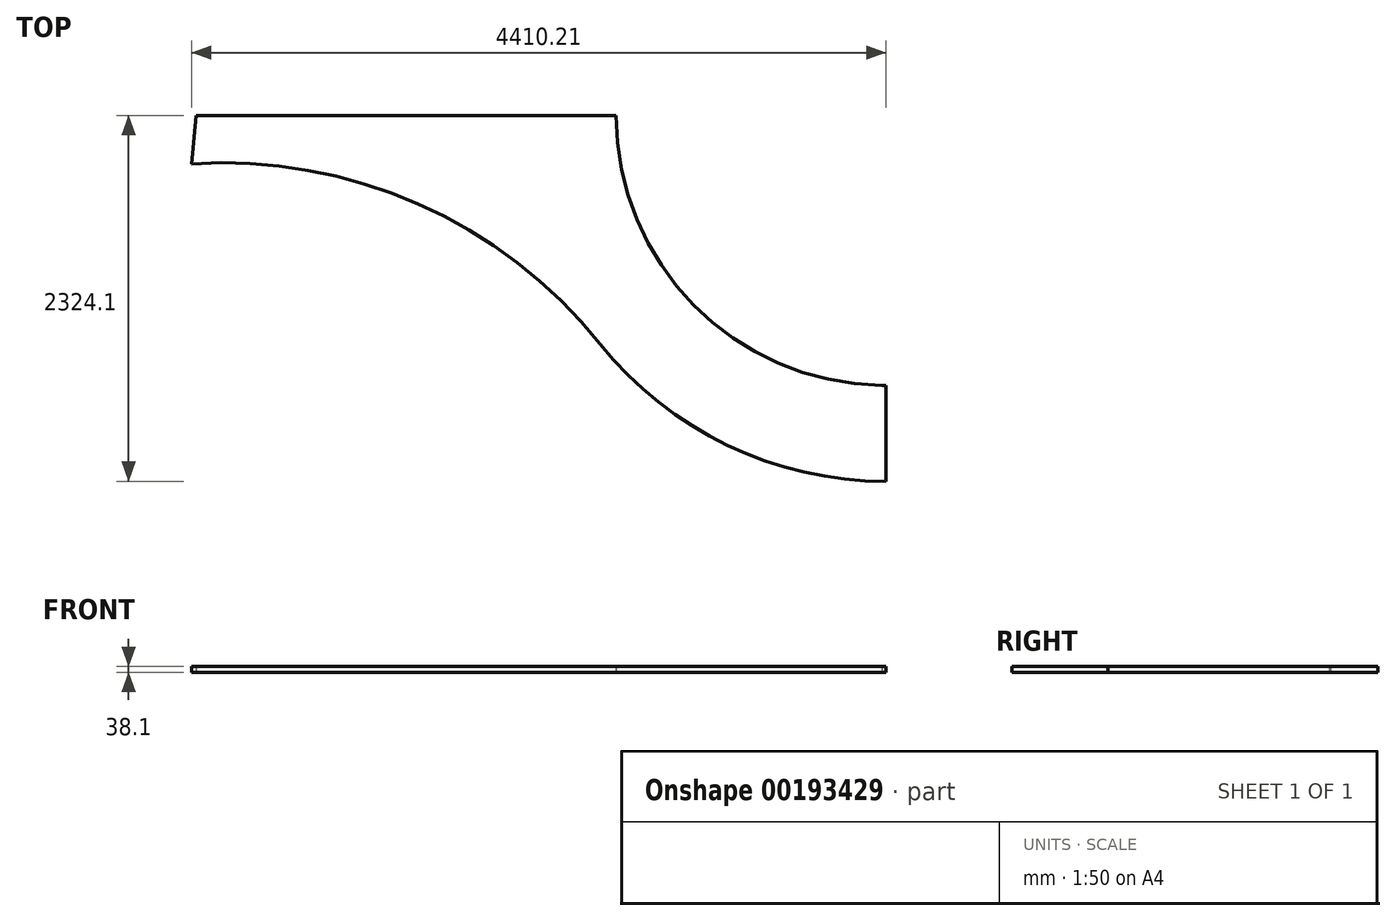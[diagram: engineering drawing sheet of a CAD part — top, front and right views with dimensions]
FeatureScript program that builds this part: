
annotation { "Feature Type Name" : "Feature", "Feature Type Description" : "" }
export const myFeature = defineFeature(function(context is Context, id is Id, definition is map)
    precondition{}
    {
        {
            var Q0;
            Q0=qCreatedBy(makeId("Top.planeOp"),FACE);
            var sketch = newSketch(context, id + "F0", { "sketchPlane" : qUnion([Q0])});
            skLineSegment(sketch, "E0", {"start": v(-2316.67, 127.82) * mm, "end": v(349.93, 127.82) * mm});
            skLineSegment(sketch, "E1", {"start": v(2064.43, -1586.68) * mm, "end": v(2064.43, -2196.28) * mm});
            skArc(sketch, "E2", {"start": v(2064.43, -1586.68) * mm, "mid": v(852.1, -1084.52) * mm, "end": v(349.93, 127.82) * mm});
            skArc(sketch, "E3.0", {"start": v(2064.43, -1891.48) * mm, "mid": v(1189.8, -1692.24) * mm, "end": v(487.77, -1133.82) * mm});
            skArc(sketch, "E4.0", {"start": v(2064.43, -2196.28) * mm, "mid": v(1057.78, -1966.96) * mm, "end": v(249.79, -1324.25) * mm});
            skLineSegment(sketch, "E5", {"start": v(-2316.67, 127.82) * mm, "end": v(-2345.78, -179.16) * mm});
            skPoint(sketch, "E6", {"position": v(-2316.67, 127.82) * mm});
            skArc(sketch, "E7", {"start": v(487.77, -1133.82) * mm, "mid": v(-608.98, -238.62) * mm, "end": v(-1976.45, 127.82) * mm});
            skArc(sketch, "E8.0", {"start": v(249.79, -1324.25) * mm, "mid": v(-907.75, -433.81) * mm, "end": v(-2345.78, -179.16) * mm});
            skPoint(sketch, "E9.orphan", {"position": v(-2436.3, -1133.82) * mm});
            skLineSegment(sketch, "E10.0", {"start": v(-2291.3, 126.27) * mm, "end": v(-2317.7, -152.02) * mm});
            skArc(sketch, "E11.0", {"start": v(300.99, -1348.25) * mm, "mid": v(-872.47, -421.75) * mm, "end": v(-2343.36, -153.55) * mm});
            skArc(sketch, "E12.0", {"start": v(2064.43, -2170.88) * mm, "mid": v(1097.91, -1957.81) * mm, "end": v(310.57, -1358.11) * mm});
            skLineSegment(sketch, "E13.0", {"start": v(2039.03, -1586.5) * mm, "end": v(2039.03, -2170.74) * mm});
            skLineSegment(sketch, "E14", {"start": v(-2343.36, -153.55) * mm, "end": v(-2316.67, 127.82) * mm});
            skLineSegment(sketch, "E15", {"start": v(-2343.36, -153.55) * mm, "end": v(-2317.7, -152.02) * mm});
            skLineSegment(sketch, "E16", {"start": v(-2291.3, 126.27) * mm, "end": v(-2316.67, 127.82) * mm});
            skLineSegment(sketch, "E17.bottom", {"start": v(2039.03, -1586.5) * mm, "end": v(2064.43, -1586.5) * mm});
            skLineSegment(sketch, "E17.top", {"start": v(2039.03, -1586.68) * mm, "end": v(2064.43, -1586.68) * mm});
            skLineSegment(sketch, "E17.left", {"start": v(2039.03, -1586.5) * mm, "end": v(2039.03, -1586.68) * mm});
            skLineSegment(sketch, "E17.right", {"start": v(2064.43, -1586.5) * mm, "end": v(2064.43, -1586.68) * mm});
            skLineSegment(sketch, "E18", {"start": v(2064.43, -2170.88) * mm, "end": v(2039.03, -2170.74) * mm});
            skLineSegment(sketch, "E19", {"start": v(300.99, -1348.25) * mm, "end": v(310.57, -1358.11) * mm});
            skSolve(sketch);
        }
        {
            var Q0;
            Q0 = qSketchRegion(id + "F0", true);
            extrude(context, id + "F1", {"entities" : qUnion([Q0]), "endBound" : BoundingType.SYMMETRIC, "depth" : 38.1 * mm});
        }
    });
